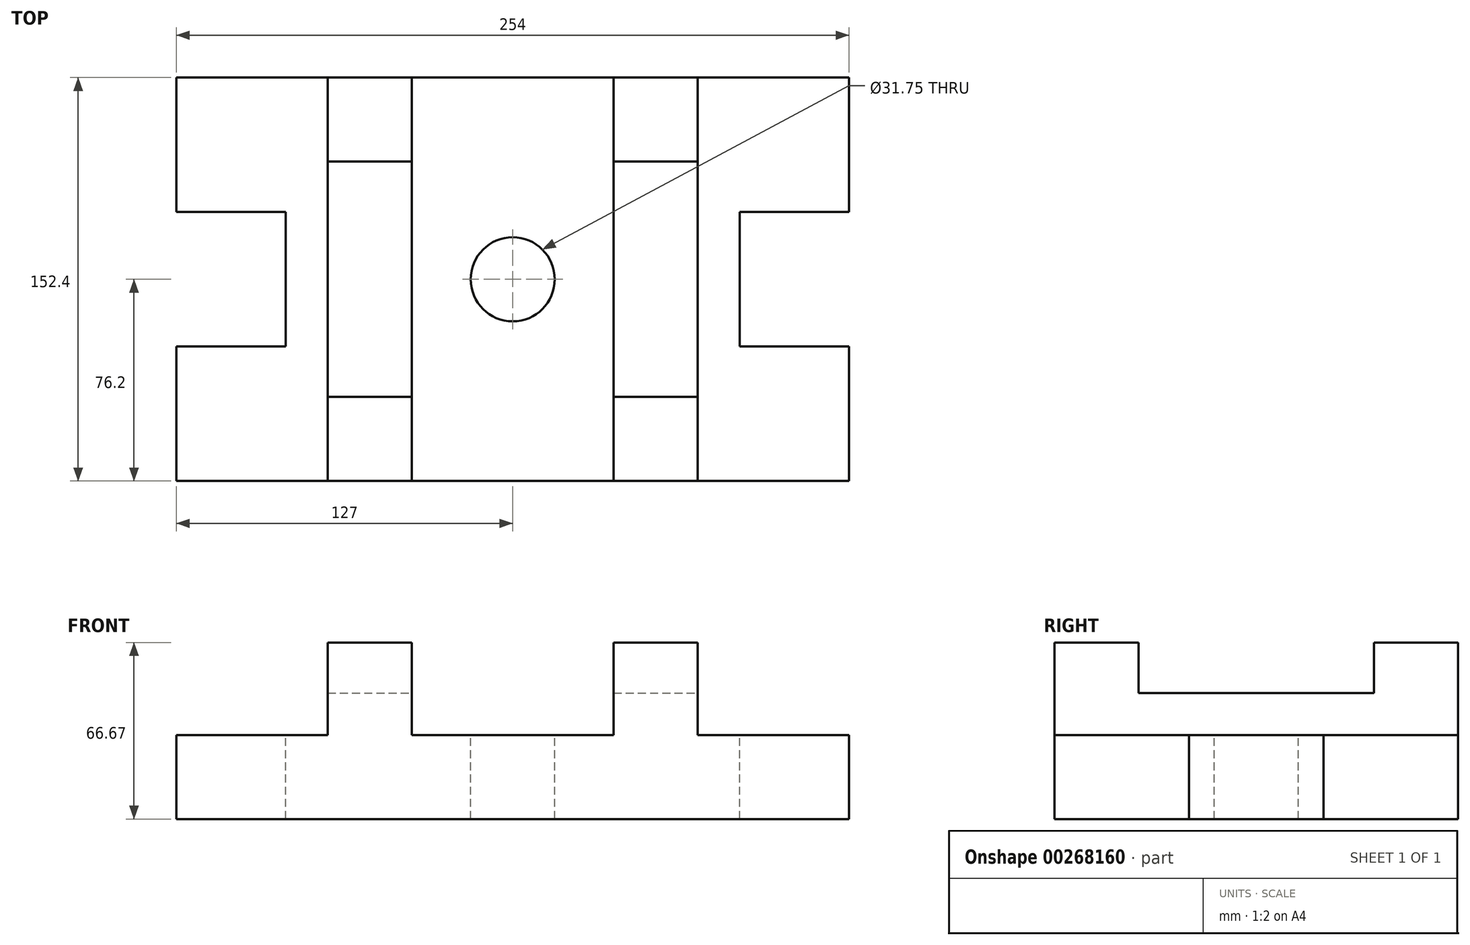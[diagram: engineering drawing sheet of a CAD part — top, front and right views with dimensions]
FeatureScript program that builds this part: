
annotation { "Feature Type Name" : "Feature", "Feature Type Description" : "" }
export const myFeature = defineFeature(function(context is Context, id is Id, definition is map)
    precondition{}
    {
        {
            var Q0;
            Q0=qCreatedBy(makeId("Top.planeOp"),FACE);
            var sketch = newSketch(context, id + "F0", { "sketchPlane" : qUnion([Q0])});
            skLineSegment(sketch, "E0.bottom", {"start": v(-127, 76.2) * mm, "end": v(127, 76.2) * mm});
            skLineSegment(sketch, "E0.top", {"start": v(-127, -76.2) * mm, "end": v(127, -76.2) * mm});
            skLineSegment(sketch, "E0.left", {"start": v(-127, 76.2) * mm, "end": v(-127, 25.4) * mm});
            skLineSegment(sketch, "E0.right", {"start": v(127, 76.2) * mm, "end": v(127, 25.4) * mm});
            skPoint(sketch, "E0.middle", {"position": v(0, 0) * mm});
            skLineSegment(sketch, "E1", {"start": v(-69.85, 76.2) * mm, "end": v(-69.85, -76.2) * mm});
            skLineSegment(sketch, "E2", {"start": v(69.85, 76.2) * mm, "end": v(69.85, -76.2) * mm});
            skLineSegment(sketch, "E3", {"start": v(-38.1, 76.2) * mm, "end": v(-38.1, -76.2) * mm});
            skLineSegment(sketch, "E4", {"start": v(38.1, 76.2) * mm, "end": v(38.1, -76.2) * mm});
            skPoint(sketch, "E5", {"position": v(-127, 25.4) * mm});
            skPoint(sketch, "E6", {"position": v(-127, -25.4) * mm});
            skLineSegment(sketch, "E7", {"start": v(-127, -25.4) * mm, "end": v(-85.72, -25.4) * mm});
            skLineSegment(sketch, "E8", {"start": v(-127, 25.4) * mm, "end": v(-85.72, 25.4) * mm});
            skLineSegment(sketch, "E9", {"start": v(-85.72, 25.4) * mm, "end": v(-85.72, -25.4) * mm});
            skPoint(sketch, "E10", {"position": v(127, 25.4) * mm});
            skPoint(sketch, "E11", {"position": v(127, -25.4) * mm});
            skLineSegment(sketch, "E12", {"start": v(127, 25.4) * mm, "end": v(85.72, 25.4) * mm});
            skLineSegment(sketch, "E13", {"start": v(127, -25.4) * mm, "end": v(85.72, -25.4) * mm});
            skLineSegment(sketch, "E14", {"start": v(85.72, 25.4) * mm, "end": v(85.72, -25.4) * mm});
            skLineSegment(sketch, "E15.trimOffspring", {"start": v(-127, -25.4) * mm, "end": v(-127, -76.2) * mm});
            skLineSegment(sketch, "E16.trimOffspring", {"start": v(127, -25.4) * mm, "end": v(127, -76.2) * mm});
            skLineSegment(sketch, "E17", {"start": v(-69.85, 44.45) * mm, "end": v(-38.1, 44.45) * mm});
            skLineSegment(sketch, "E18", {"start": v(-69.85, -44.45) * mm, "end": v(-38.1, -44.45) * mm});
            skLineSegment(sketch, "E19", {"start": v(38.1, 44.45) * mm, "end": v(69.85, 44.45) * mm});
            skLineSegment(sketch, "E20", {"start": v(38.1, -44.45) * mm, "end": v(69.85, -44.45) * mm});
            skCircle(sketch, "E21", {"center": v(0, 0) * mm, "radius": 15.88 * mm});
            skSolve(sketch);
        }
        {
            var Q0;
            Q0 = qSketchRegion(id + "F0", true);
            var Q1;
            {var subQ0=sQuery(id+"F0.wireOp",EDGE,"E17");Q1=makeQuery(id+"F0.imprint","IMPRINT",FACE,{"disambiguationData":[TD([[makeQuery(id+"F0.imprint","IMPRINT",EDGE,{"derivedFrom":subQ0}),-1.0]])]});}
            var Q2;
            {var subQ0=sQuery(id+"F0.wireOp",EDGE,"E19");Q2=makeQuery(id+"F0.imprint","IMPRINT",FACE,{"disambiguationData":[TD([[makeQuery(id+"F0.imprint","IMPRINT",EDGE,{"derivedFrom":subQ0}),-1.0]])]});}
            extrude(context, id + "F1", {"entities" : qUnion([Q0, Q1, Q2]), "oppositeDirection" : true, "depth" : 31.75 * mm});
        }
        {
            var Q0;
            {var subQ5=sQuery(id+"F0.wireOp",EDGE,"E17");Q0=makeQuery(id+"F0.imprint","IMPRINT",FACE,{"disambiguationData":[TD([[makeQuery(id+"F0.imprint","IMPRINT",EDGE,{"derivedFrom":subQ5}),1.0]])]});}
            var Q1;
            {var subQ5=sQuery(id+"F0.wireOp",EDGE,"E18");Q1=makeQuery(id+"F0.imprint","IMPRINT",FACE,{"disambiguationData":[TD([[makeQuery(id+"F0.imprint","IMPRINT",EDGE,{"derivedFrom":subQ5}),-1.0]])]});}
            var Q2;
            {var subQ5=sQuery(id+"F0.wireOp",EDGE,"E19");Q2=makeQuery(id+"F0.imprint","IMPRINT",FACE,{"disambiguationData":[TD([[makeQuery(id+"F0.imprint","IMPRINT",EDGE,{"derivedFrom":subQ5}),1.0]])]});}
            var Q3;
            {var subQ5=sQuery(id+"F0.wireOp",EDGE,"E20");Q3=makeQuery(id+"F0.imprint","IMPRINT",FACE,{"disambiguationData":[TD([[makeQuery(id+"F0.imprint","IMPRINT",EDGE,{"derivedFrom":subQ5}),-1.0]])]});}
            extrude(context, id + "F2", {"entities" : qUnion([Q0, Q1, Q2, Q3]), "operationType" : NewBodyOperationType.ADD, "depth" : 34.92 * mm});
        }
        {
            var Q0;
            {var subQ0=sQuery(id+"F0.wireOp",EDGE,"E17");Q0=makeQuery(id+"F0.imprint","IMPRINT",FACE,{"disambiguationData":[TD([[makeQuery(id+"F0.imprint","IMPRINT",EDGE,{"derivedFrom":subQ0}),-1.0]])]});}
            var Q1;
            {var subQ0=sQuery(id+"F0.wireOp",EDGE,"E19");Q1=makeQuery(id+"F0.imprint","IMPRINT",FACE,{"disambiguationData":[TD([[makeQuery(id+"F0.imprint","IMPRINT",EDGE,{"derivedFrom":subQ0}),-1.0]])]});}
            extrude(context, id + "F3", {"entities" : qUnion([Q0, Q1]), "operationType" : NewBodyOperationType.ADD, "depth" : 15.88 * mm});
        }
    });
